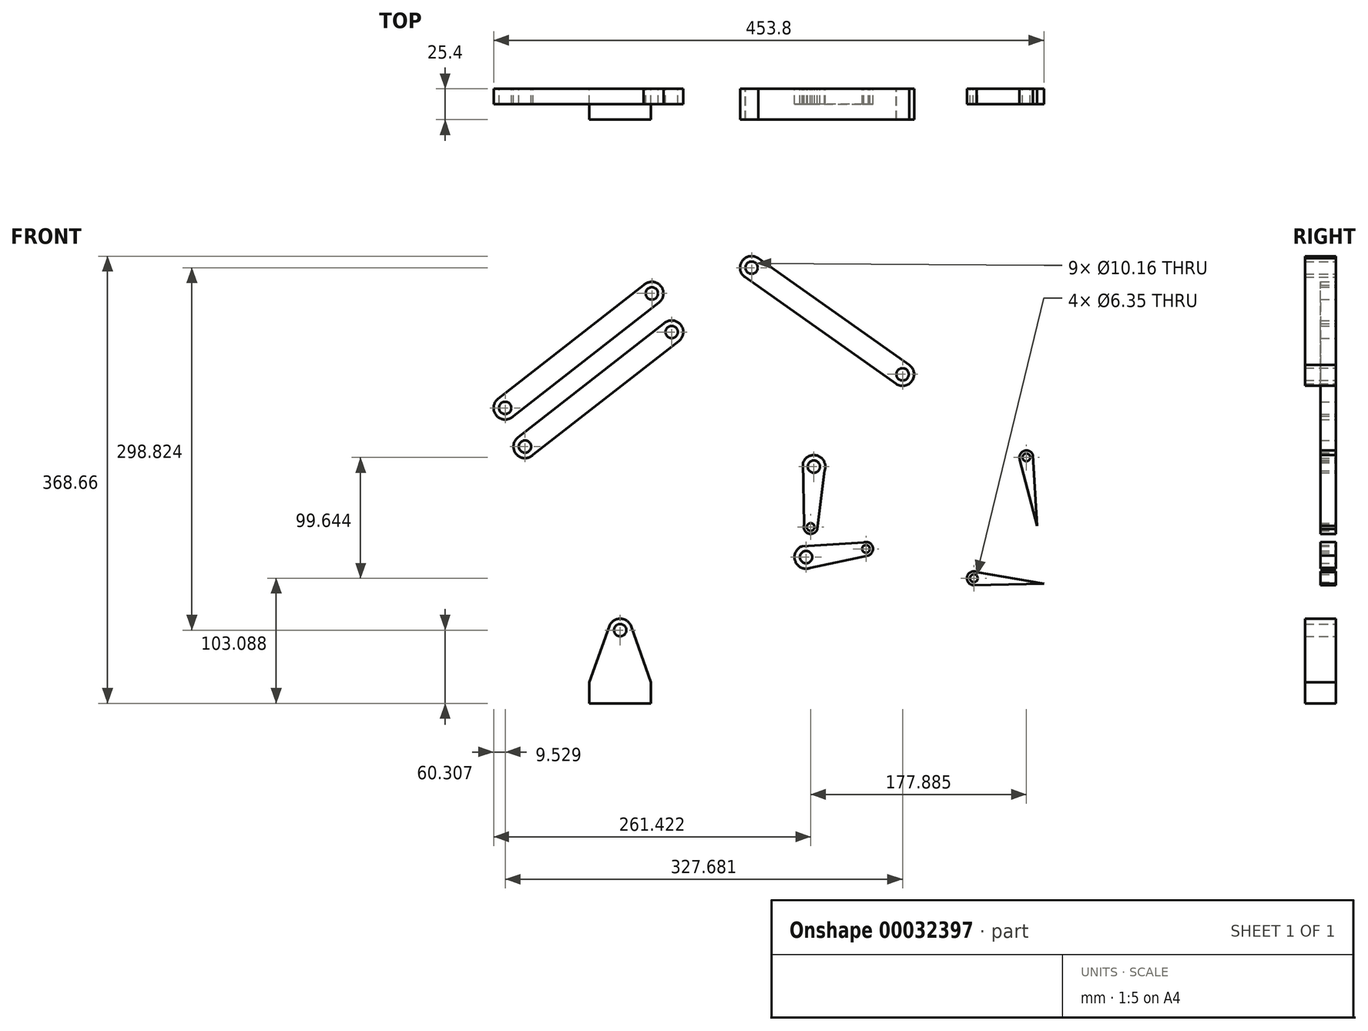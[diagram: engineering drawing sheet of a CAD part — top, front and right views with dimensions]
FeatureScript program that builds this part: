
annotation { "Feature Type Name" : "Feature", "Feature Type Description" : "" }
export const myFeature = defineFeature(function(context is Context, id is Id, definition is map)
    precondition{}
    {
        {
            var Q0;
            Q0=qCreatedBy(makeId("Front.planeOp"),FACE);
            var sketch = newSketch(context, id + "F0", { "sketchPlane" : qUnion([Q0])});
            skLineSegment(sketch, "E0.bottom", {"start": v(-998.78, -379.39) * mm, "end": v(-947.98, -379.39) * mm});
            skLineSegment(sketch, "E0.top", {"start": v(-998.78, -362.11) * mm, "end": v(-947.98, -362.11) * mm});
            skLineSegment(sketch, "E0.left", {"start": v(-998.78, -379.39) * mm, "end": v(-998.78, -362.11) * mm});
            skLineSegment(sketch, "E0.right", {"start": v(-947.98, -379.39) * mm, "end": v(-947.98, -362.11) * mm});
            skLineSegment(sketch, "E1", {"start": v(-973.38, -379.39) * mm, "end": v(-973.38, -319.07) * mm, "construction": true});
            skCircle(sketch, "E2", {"center": v(-973.38, -319.07) * mm, "radius": 9.53 * mm});
            skCircle(sketch, "E3", {"center": v(-973.38, -319.07) * mm, "radius": 5.08 * mm});
            skLineSegment(sketch, "E4", {"start": v(-998.78, -362.11) * mm, "end": v(-982.35, -315.89) * mm});
            skLineSegment(sketch, "E5", {"start": v(-947.98, -362.11) * mm, "end": v(-964.4, -315.89) * mm});
            skCircle(sketch, "E6", {"center": v(-852.43, -224.64) * mm, "radius": 9.53 * mm});
            skCircle(sketch, "E7", {"center": v(-852.43, -224.64) * mm, "radius": 5.08 * mm});
            skLineSegment(sketch, "E8", {"start": v(-846.56, -232.14) * mm, "end": v(-859.1, -217.84) * mm, "construction": true});
            skLineSegment(sketch, "E9", {"start": v(-966.72, -325.88) * mm, "end": v(-979.25, -311.58) * mm, "construction": true});
            skLineSegment(sketch, "E10", {"start": v(-846.56, -232.14) * mm, "end": v(-966.72, -325.88) * mm});
            skLineSegment(sketch, "E11", {"start": v(-979.25, -311.58) * mm, "end": v(-859.1, -217.84) * mm});
            skCircle(sketch, "E12", {"center": v(-727.95, -312.56) * mm, "radius": 9.53 * mm});
            skCircle(sketch, "E13", {"center": v(-727.95, -312.56) * mm, "radius": 5.08 * mm});
            skLineSegment(sketch, "E14", {"start": v(-733.34, -320.4) * mm, "end": v(-722.55, -304.7) * mm, "construction": true});
            skLineSegment(sketch, "E15", {"start": v(-857.83, -232.5) * mm, "end": v(-847.04, -216.8) * mm, "construction": true});
            skLineSegment(sketch, "E16", {"start": v(-857.83, -232.5) * mm, "end": v(-733.34, -320.4) * mm});
            skLineSegment(sketch, "E17", {"start": v(-722.55, -304.7) * mm, "end": v(-847.04, -216.8) * mm});
            skCircle(sketch, "E18", {"center": v(-730.57, -362.28) * mm, "radius": 5.72 * mm});
            skCircle(sketch, "E19", {"center": v(-730.57, -362.28) * mm, "radius": 3.18 * mm});
            skCircle(sketch, "E20", {"center": v(-678.5, -305.8) * mm, "radius": 5.72 * mm});
            skCircle(sketch, "E21", {"center": v(-678.5, -305.8) * mm, "radius": 3.18 * mm});
            skLineSegment(sketch, "E22", {"start": v(-725.14, -364.06) * mm, "end": v(-735.85, -360.11) * mm, "construction": true});
            skLineSegment(sketch, "E23", {"start": v(-719.03, -315.91) * mm, "end": v(-736.9, -309.32) * mm, "construction": true});
            skLineSegment(sketch, "E24", {"start": v(-719.03, -315.91) * mm, "end": v(-725.14, -364.06) * mm});
            skLineSegment(sketch, "E25", {"start": v(-736.9, -309.32) * mm, "end": v(-735.85, -360.11) * mm});
            skLineSegment(sketch, "E26", {"start": v(-731.15, -303.59) * mm, "end": v(-724.57, -321.46) * mm, "construction": true});
            skLineSegment(sketch, "E27", {"start": v(-680.44, -300.43) * mm, "end": v(-676.5, -311.15) * mm, "construction": true});
            skLineSegment(sketch, "E28", {"start": v(-724.57, -321.46) * mm, "end": v(-676.5, -311.15) * mm});
            skLineSegment(sketch, "E29", {"start": v(-680.44, -300.43) * mm, "end": v(-731.15, -303.59) * mm});
            skLineSegment(sketch, "E30", {"start": v(-725.14, -364.06) * mm, "end": v(-676.5, -311.15) * mm, "construction": true});
            skLineSegment(sketch, "E31", {"start": v(-700.82, -337.6) * mm, "end": v(-670.45, -365.52) * mm, "construction": true});
            skLineSegment(sketch, "E32", {"start": v(-728.14, -357.1) * mm, "end": v(-731.15, -367.96) * mm, "construction": true});
            skLineSegment(sketch, "E33", {"start": v(-683.84, -307.85) * mm, "end": v(-673.1, -303.94) * mm, "construction": true});
            skLineSegment(sketch, "E34", {"start": v(-731.15, -367.96) * mm, "end": v(-672.75, -366.6) * mm});
            skLineSegment(sketch, "E35", {"start": v(-672.75, -366.6) * mm, "end": v(-728.14, -357.1) * mm});
            skLineSegment(sketch, "E36", {"start": v(-673.1, -303.94) * mm, "end": v(-669.77, -362.26) * mm});
            skLineSegment(sketch, "E37", {"start": v(-669.77, -362.26) * mm, "end": v(-683.84, -307.85) * mm});
            skCircle(sketch, "E38", {"center": v(-1058.1, -245.07) * mm, "radius": 9.53 * mm});
            skCircle(sketch, "E39", {"center": v(-1058.1, -245.07) * mm, "radius": 5.08 * mm});
            skLineSegment(sketch, "E40", {"start": v(-931.27, -158.14) * mm, "end": v(-1051.43, -251.88) * mm});
            skLineSegment(sketch, "E41", {"start": v(-1063.97, -237.58) * mm, "end": v(-943.8, -143.84) * mm});
            skCircle(sketch, "E42", {"center": v(-937.15, -150.64) * mm, "radius": 9.53 * mm});
            skCircle(sketch, "E43", {"center": v(-937.15, -150.64) * mm, "radius": 5.08 * mm});
            skCircle(sketch, "E44", {"center": v(-669.49, -228.78) * mm, "radius": 5.08 * mm});
            skCircle(sketch, "E45", {"center": v(-669.49, -228.78) * mm, "radius": 9.53 * mm});
            skLineSegment(sketch, "E46", {"start": v(-664.09, -220.93) * mm, "end": v(-788.58, -133.01) * mm});
            skLineSegment(sketch, "E47", {"start": v(-799.37, -148.71) * mm, "end": v(-674.88, -236.63) * mm});
            skCircle(sketch, "E48", {"center": v(-793.97, -140.86) * mm, "radius": 9.53 * mm});
            skCircle(sketch, "E49", {"center": v(-793.97, -140.86) * mm, "radius": 5.08 * mm});
            skCircle(sketch, "E50", {"center": v(-730.41, -217.35) * mm, "radius": 5.08 * mm});
            skCircle(sketch, "E51", {"center": v(-730.41, -217.35) * mm, "radius": 9.53 * mm});
            skLineSegment(sketch, "E52", {"start": v(-725.01, -209.5) * mm, "end": v(-849.5, -121.6) * mm});
            skLineSegment(sketch, "E53", {"start": v(-860.3, -137.29) * mm, "end": v(-735.8, -225.2) * mm});
            skCircle(sketch, "E54", {"center": v(-854.9, -129.44) * mm, "radius": 9.53 * mm});
            skCircle(sketch, "E55", {"center": v(-854.9, -129.44) * mm, "radius": 5.08 * mm});
            skLineSegment(sketch, "E56", {"start": v(-806.62, -376.96) * mm, "end": v(-758.55, -366.64) * mm});
            skLineSegment(sketch, "E57", {"start": v(-762.5, -355.92) * mm, "end": v(-813.2, -359.08) * mm});
            skCircle(sketch, "E58", {"center": v(-760.56, -361.3) * mm, "radius": 5.72 * mm});
            skCircle(sketch, "E59", {"center": v(-760.56, -361.3) * mm, "radius": 3.18 * mm});
            skCircle(sketch, "E60", {"center": v(-810, -368.05) * mm, "radius": 9.53 * mm});
            skCircle(sketch, "E61", {"center": v(-810, -368.05) * mm, "radius": 5.08 * mm});
            skLineSegment(sketch, "E62", {"start": v(-794.66, -296.83) * mm, "end": v(-800.77, -344.98) * mm});
            skLineSegment(sketch, "E63", {"start": v(-812.53, -290.23) * mm, "end": v(-811.48, -341.02) * mm});
            skCircle(sketch, "E64", {"center": v(-803.58, -293.47) * mm, "radius": 9.53 * mm});
            skCircle(sketch, "E65", {"center": v(-803.58, -293.47) * mm, "radius": 5.08 * mm});
            skCircle(sketch, "E66", {"center": v(-806.2, -343.2) * mm, "radius": 3.18 * mm});
            skCircle(sketch, "E67", {"center": v(-806.2, -343.2) * mm, "radius": 5.72 * mm});
            skCircle(sketch, "E68", {"center": v(-671.63, -385.48) * mm, "radius": 3.18 * mm});
            skCircle(sketch, "E69", {"center": v(-671.63, -385.48) * mm, "radius": 5.72 * mm});
            skLineSegment(sketch, "E70", {"start": v(-672.22, -391.17) * mm, "end": v(-613.82, -389.8) * mm});
            skLineSegment(sketch, "E71", {"start": v(-613.82, -389.8) * mm, "end": v(-669.2, -380.3) * mm});
            skCircle(sketch, "E72", {"center": v(-628.31, -285.84) * mm, "radius": 3.18 * mm});
            skCircle(sketch, "E73", {"center": v(-628.31, -285.84) * mm, "radius": 5.72 * mm});
            skLineSegment(sketch, "E74", {"start": v(-622.91, -283.97) * mm, "end": v(-619.58, -342.3) * mm});
            skLineSegment(sketch, "E75", {"start": v(-619.58, -342.3) * mm, "end": v(-633.65, -287.88) * mm});
            skLineSegment(sketch, "E76", {"start": v(-937.86, -471.3) * mm, "end": v(-954.29, -425.07) * mm});
            skCircle(sketch, "E77", {"center": v(-963.26, -428.26) * mm, "radius": 9.53 * mm});
            skCircle(sketch, "E78", {"center": v(-963.26, -428.26) * mm, "radius": 5.08 * mm});
            skLineSegment(sketch, "E79", {"start": v(-988.66, -471.3) * mm, "end": v(-972.24, -425.07) * mm});
            skLineSegment(sketch, "E80.top", {"start": v(-988.66, -471.3) * mm, "end": v(-937.86, -471.3) * mm});
            skLineSegment(sketch, "E80.left", {"start": v(-988.66, -488.57) * mm, "end": v(-988.66, -471.3) * mm});
            skLineSegment(sketch, "E80.right", {"start": v(-937.86, -488.57) * mm, "end": v(-937.86, -471.3) * mm});
            skLineSegment(sketch, "E80.bottom", {"start": v(-988.66, -488.57) * mm, "end": v(-937.86, -488.57) * mm});
            skCircle(sketch, "E81", {"center": v(-920.76, -182.49) * mm, "radius": 5.08 * mm});
            skCircle(sketch, "E82", {"center": v(-920.76, -182.49) * mm, "radius": 9.53 * mm});
            skCircle(sketch, "E83", {"center": v(-1041.7, -276.92) * mm, "radius": 5.08 * mm});
            skLineSegment(sketch, "E84", {"start": v(-914.88, -189.98) * mm, "end": v(-1035.04, -283.73) * mm});
            skCircle(sketch, "E85", {"center": v(-1041.7, -276.92) * mm, "radius": 9.53 * mm});
            skLineSegment(sketch, "E86", {"start": v(-1047.58, -269.42) * mm, "end": v(-927.42, -175.68) * mm});
            skSolve(sketch);
        }
        {
            var Q0;
            {var subQ2=sQuery(id+"F0.wireOp",EDGE,"E76");Q0=makeQuery(id+"F0.imprint","IMPRINT",FACE,{"disambiguationData":[TD([[makeQuery(id+"F0.imprint","IMPRINT",EDGE,{"derivedFrom":subQ2}),1.0]])]});}
            var Q1;
            Q1=makeQuery(id+"F0.imprint","IMPRINT",FACE,{"disambiguationData":[TD([[makeQuery(id+"F0.imprint","IMPRINT",EDGE,{"derivedFrom":sQuery(id+"F0.wireOp",EDGE,"E78")}),-1.0]])]});
            var Q2;
            Q2=makeQuery(id+"F0.imprint","IMPRINT",FACE,{"disambiguationData":[TD([[makeQuery(id+"F0.imprint","IMPRINT",EDGE,{"derivedFrom":sQuery(id+"F0.wireOp",EDGE,"E80.top")}),-1.0]])]});
            extrude(context, id + "F1", {"entities" : qUnion([Q0, Q1, Q2]), "depth" : 25.4 * mm});
        }
        {
            var Q0;
            {var subQ1=sQuery(id+"F0.wireOp",EDGE,"E40");var subQ5=sQuery(id+"F0.wireOp",EDGE,"E38");var subQ7=makeQuery(id+"F0.imprint","INTERSECT",VERTEX,{"derivedFrom":[subQ5,subQ1]});Q0=makeQuery(id+"F0.imprint","IMPRINT",FACE,{"disambiguationData":[TD([[makeQuery(id+"F0.imprint","IMPRINT",EDGE,{"disambiguationData":[TD([[subQ7,-1.0]])],"derivedFrom":subQ5}),-1.0]])]});}
            var Q1;
            Q1=makeQuery(id+"F0.imprint","IMPRINT",FACE,{"disambiguationData":[TD([[makeQuery(id+"F0.imprint","IMPRINT",EDGE,{"derivedFrom":sQuery(id+"F0.wireOp",EDGE,"E43")}),-1.0]])]});
            var Q2;
            Q2=makeQuery(id+"F0.imprint","IMPRINT",FACE,{"disambiguationData":[TD([[makeQuery(id+"F0.imprint","IMPRINT",EDGE,{"derivedFrom":sQuery(id+"F0.wireOp",EDGE,"E39")}),-1.0]])]});
            extrude(context, id + "F2", {"entities" : qUnion([Q0, Q1, Q2]), "depth" : 12.7 * mm});
        }
        {
            var Q0;
            {var subQ0=sQuery(id+"F0.wireOp",EDGE,"E86");var subQ3=sQuery(id+"F0.wireOp",EDGE,"E82");var subQ4=makeQuery(id+"F0.imprint","INTERSECT",VERTEX,{"derivedFrom":[subQ3,subQ0]});Q0=makeQuery(id+"F0.imprint","IMPRINT",FACE,{"disambiguationData":[TD([[makeQuery(id+"F0.imprint","IMPRINT",EDGE,{"disambiguationData":[TD([[subQ4,-1.0]])],"derivedFrom":subQ3}),-1.0]])]});}
            var Q1;
            Q1=makeQuery(id+"F0.imprint","IMPRINT",FACE,{"disambiguationData":[TD([[makeQuery(id+"F0.imprint","IMPRINT",EDGE,{"derivedFrom":sQuery(id+"F0.wireOp",EDGE,"E83")}),-1.0]])]});
            var Q2;
            Q2=makeQuery(id+"F0.imprint","IMPRINT",FACE,{"disambiguationData":[TD([[makeQuery(id+"F0.imprint","IMPRINT",EDGE,{"derivedFrom":sQuery(id+"F0.wireOp",EDGE,"E81")}),-1.0]])]});
            extrude(context, id + "F3", {"entities" : qUnion([Q0, Q1, Q2]), "depth" : 12.7 * mm});
        }
        {
            var Q0;
            {var subQ1=sQuery(id+"F0.wireOp",EDGE,"E52");var subQ5=sQuery(id+"F0.wireOp",EDGE,"E51");var subQ7=makeQuery(id+"F0.imprint","INTERSECT",VERTEX,{"derivedFrom":[subQ5,subQ1]});Q0=makeQuery(id+"F0.imprint","IMPRINT",FACE,{"disambiguationData":[TD([[makeQuery(id+"F0.imprint","IMPRINT",EDGE,{"disambiguationData":[TD([[subQ7,-1.0]])],"derivedFrom":subQ5}),-1.0]])]});}
            var Q1;
            Q1=makeQuery(id+"F0.imprint","IMPRINT",FACE,{"disambiguationData":[TD([[makeQuery(id+"F0.imprint","IMPRINT",EDGE,{"derivedFrom":sQuery(id+"F0.wireOp",EDGE,"E55")}),-1.0]])]});
            var Q2;
            Q2=makeQuery(id+"F0.imprint","IMPRINT",FACE,{"disambiguationData":[TD([[makeQuery(id+"F0.imprint","IMPRINT",EDGE,{"derivedFrom":sQuery(id+"F0.wireOp",EDGE,"E50")}),-1.0]])]});
            extrude(context, id + "F4", {"entities" : qUnion([Q0, Q1, Q2]), "depth" : 25.4 * mm});
        }
        {
            var Q0;
            {var subQ1=sQuery(id+"F0.wireOp",EDGE,"E62");var subQ5=sQuery(id+"F0.wireOp",EDGE,"E64");var subQ7=makeQuery(id+"F0.imprint","INTERSECT",VERTEX,{"derivedFrom":[subQ1,subQ5]});Q0=makeQuery(id+"F0.imprint","IMPRINT",FACE,{"disambiguationData":[TD([[makeQuery(id+"F0.imprint","IMPRINT",EDGE,{"disambiguationData":[TD([[subQ7,-1.0]])],"derivedFrom":subQ1}),-1.0]])]});}
            var Q1;
            Q1=makeQuery(id+"F0.imprint","IMPRINT",FACE,{"disambiguationData":[TD([[makeQuery(id+"F0.imprint","IMPRINT",EDGE,{"derivedFrom":sQuery(id+"F0.wireOp",EDGE,"E65")}),-1.0]])]});
            var Q2;
            Q2=makeQuery(id+"F0.imprint","IMPRINT",FACE,{"disambiguationData":[TD([[makeQuery(id+"F0.imprint","IMPRINT",EDGE,{"derivedFrom":sQuery(id+"F0.wireOp",EDGE,"E66")}),-1.0]])]});
            extrude(context, id + "F5", {"entities" : qUnion([Q0, Q1, Q2]), "depth" : 12.7 * mm});
        }
        {
            var Q0;
            {var subQ0=sQuery(id+"F0.wireOp",EDGE,"E60");var subQ3=sQuery(id+"F0.wireOp",EDGE,"E56");var subQ4=makeQuery(id+"F0.imprint","INTERSECT",VERTEX,{"derivedFrom":[subQ3,subQ0]});Q0=makeQuery(id+"F0.imprint","IMPRINT",FACE,{"disambiguationData":[TD([[makeQuery(id+"F0.imprint","IMPRINT",EDGE,{"disambiguationData":[TD([[subQ4,-1.0]])],"derivedFrom":subQ3}),1.0]])]});}
            var Q1;
            Q1=makeQuery(id+"F0.imprint","IMPRINT",FACE,{"disambiguationData":[TD([[makeQuery(id+"F0.imprint","IMPRINT",EDGE,{"derivedFrom":sQuery(id+"F0.wireOp",EDGE,"E61")}),-1.0]])]});
            var Q2;
            Q2=makeQuery(id+"F0.imprint","IMPRINT",FACE,{"disambiguationData":[TD([[makeQuery(id+"F0.imprint","IMPRINT",EDGE,{"derivedFrom":sQuery(id+"F0.wireOp",EDGE,"E59")}),-1.0]])]});
            extrude(context, id + "F6", {"entities" : qUnion([Q0, Q1, Q2]), "depth" : 12.7 * mm});
        }
        {
            var Q0;
            {var subQ0=sQuery(id+"F0.wireOp",EDGE,"E75");Q0=makeQuery(id+"F0.imprint","IMPRINT",FACE,{"disambiguationData":[TD([[makeQuery(id+"F0.imprint","IMPRINT",EDGE,{"derivedFrom":subQ0}),-1.0]])]});}
            var Q1;
            Q1=makeQuery(id+"F0.imprint","IMPRINT",FACE,{"disambiguationData":[TD([[makeQuery(id+"F0.imprint","IMPRINT",EDGE,{"derivedFrom":sQuery(id+"F0.wireOp",EDGE,"E72")}),-1.0]])]});
            extrude(context, id + "F7", {"entities" : qUnion([Q0, Q1]), "depth" : 12.7 * mm});
        }
        {
            var Q0;
            {var subQ0=sQuery(id+"F0.wireOp",EDGE,"E71");Q0=makeQuery(id+"F0.imprint","IMPRINT",FACE,{"disambiguationData":[TD([[makeQuery(id+"F0.imprint","IMPRINT",EDGE,{"derivedFrom":subQ0}),1.0]])]});}
            var Q1;
            Q1=makeQuery(id+"F0.imprint","IMPRINT",FACE,{"disambiguationData":[TD([[makeQuery(id+"F0.imprint","IMPRINT",EDGE,{"derivedFrom":sQuery(id+"F0.wireOp",EDGE,"E68")}),-1.0]])]});
            extrude(context, id + "F8", {"entities" : qUnion([Q0, Q1]), "depth" : 12.7 * mm});
        }
    });
